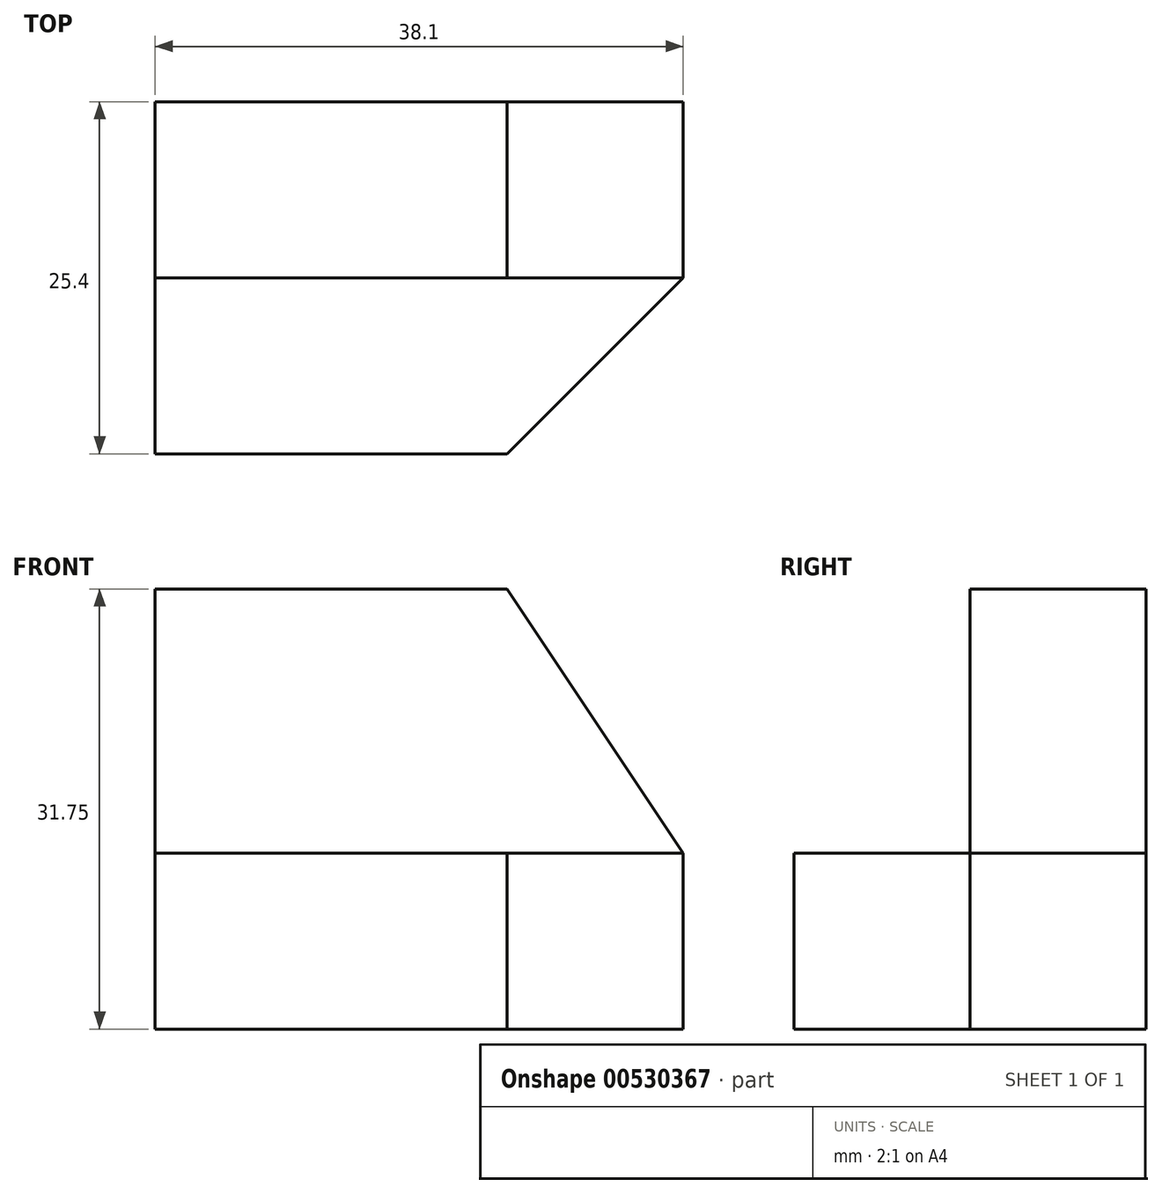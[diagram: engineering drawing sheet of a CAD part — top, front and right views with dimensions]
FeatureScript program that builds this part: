
annotation { "Feature Type Name" : "Feature", "Feature Type Description" : "" }
export const myFeature = defineFeature(function(context is Context, id is Id, definition is map)
    precondition{}
    {
        {
            var Q0;
            Q0=qCreatedBy(makeId("Right.planeOp"),FACE);
            var sketch = newSketch(context, id + "F0", { "sketchPlane" : qUnion([Q0])});
            skLineSegment(sketch, "E0", {"start": v(0, 31.75) * mm, "end": v(12.7, 31.75) * mm});
            skLineSegment(sketch, "E1", {"start": v(12.7, 31.75) * mm, "end": v(12.7, 0) * mm});
            skLineSegment(sketch, "E2", {"start": v(12.7, 0) * mm, "end": v(-12.7, 0) * mm});
            skLineSegment(sketch, "E3", {"start": v(-12.7, 0) * mm, "end": v(-12.7, 12.7) * mm});
            skLineSegment(sketch, "E4", {"start": v(-12.7, 12.7) * mm, "end": v(0, 12.7) * mm});
            skLineSegment(sketch, "E5", {"start": v(0, 12.7) * mm, "end": v(0, 31.75) * mm});
            skSolve(sketch);
        }
        {
            var Q0;
            Q0 = qSketchRegion(id + "F0", true);
            extrude(context, id + "F1", {"entities" : qUnion([Q0]), "oppositeDirection" : true, "depth" : 38.1 * mm, "offsetDistance" : 25.4 * mm});
        }
        {
            var Q0;
            Q0=qCreatedBy(makeId("Front.planeOp"),FACE);
            var sketch = newSketch(context, id + "F2", { "sketchPlane" : qUnion([Q0])});
            skLineSegment(sketch, "E6", {"start": v(0, 12.7) * mm, "end": v(0, 31.75) * mm});
            skLineSegment(sketch, "E7", {"start": v(0, 31.75) * mm, "end": v(-12.7, 31.75) * mm});
            skLineSegment(sketch, "E8", {"start": v(-12.7, 31.75) * mm, "end": v(0, 12.7) * mm});
            skSolve(sketch);
        }
        {
            var Q0;
            Q0 = qSketchRegion(id + "F2", true);
            extrude(context, id + "F3", {"entities" : qUnion([Q0]), "operationType" : NewBodyOperationType.REMOVE, "oppositeDirection" : true, "depth" : 25.4 * mm, "offsetDistance" : 25.4 * mm, "hasSecondDirection" : true, "secondDirectionOppositeDirection" : false, "secondDirectionDepth" : 12.7 * mm});
        }
        {
            var Q0;
            Q0=qCreatedBy(makeId("Top.planeOp"),FACE);
            var sketch = newSketch(context, id + "F4", { "sketchPlane" : qUnion([Q0])});
            skLineSegment(sketch, "E9", {"start": v(0, 0) * mm, "end": v(-12.7, -12.7) * mm});
            skLineSegment(sketch, "E10", {"start": v(-12.7, -12.7) * mm, "end": v(0, -12.7) * mm});
            skLineSegment(sketch, "E11", {"start": v(0, -12.7) * mm, "end": v(0, 0) * mm});
            skSolve(sketch);
        }
        {
            var Q0;
            Q0 = qSketchRegion(id + "F4", true);
            extrude(context, id + "F5", {"entities" : qUnion([Q0]), "operationType" : NewBodyOperationType.REMOVE, "oppositeDirection" : true, "depth" : 25.4 * mm, "offsetDistance" : 25.4 * mm, "hasSecondDirection" : true, "secondDirectionOppositeDirection" : false, "secondDirectionDepth" : 12.7 * mm});
        }
    });
